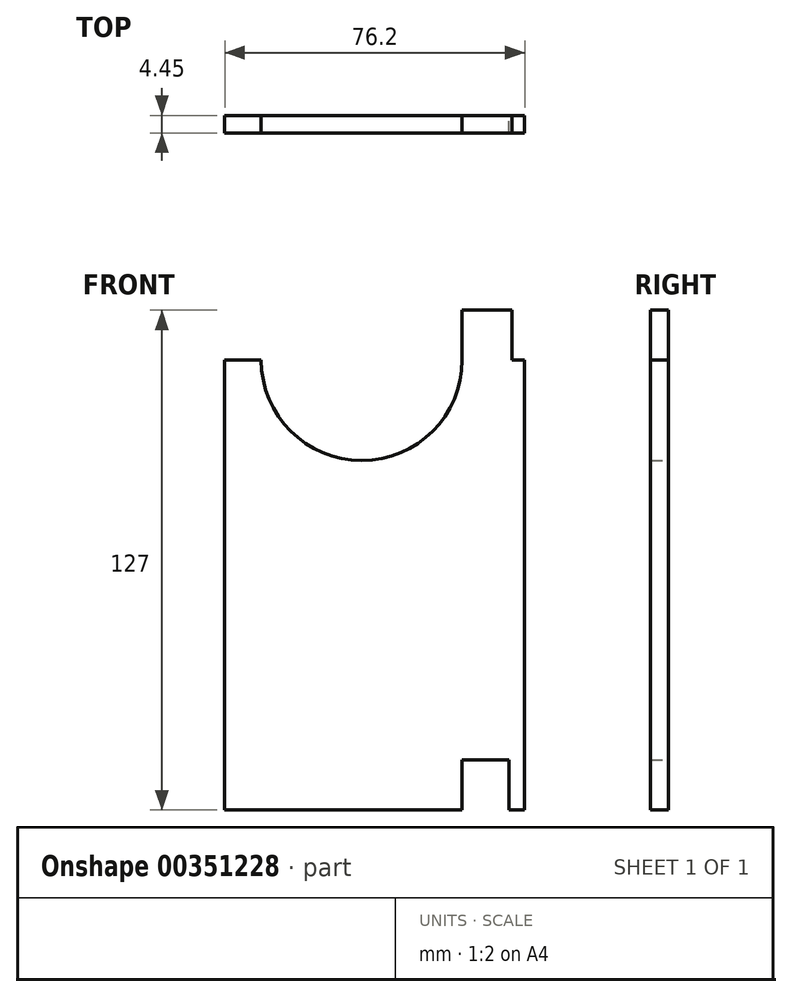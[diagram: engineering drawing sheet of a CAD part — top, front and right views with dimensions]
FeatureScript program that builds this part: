
annotation { "Feature Type Name" : "Feature", "Feature Type Description" : "" }
export const myFeature = defineFeature(function(context is Context, id is Id, definition is map)
    precondition{}
    {
        {
            var Q0;
            Q0=qCreatedBy(makeId("Front.planeOp"),FACE);
            var sketch = newSketch(context, id + "F0", { "sketchPlane" : qUnion([Q0])});
            skLineSegment(sketch, "E0", {"start": v(-43.64, 217.3) * mm, "end": v(-43.64, 103) * mm});
            skLineSegment(sketch, "E1", {"start": v(-43.64, 103) * mm, "end": v(16.68, 103) * mm});
            skLineSegment(sketch, "E2", {"start": v(32.56, 103) * mm, "end": v(32.56, 217.3) * mm});
            skLineSegment(sketch, "E3", {"start": v(32.56, 217.3) * mm, "end": v(29.38, 217.3) * mm});
            skLineSegment(sketch, "E4", {"start": v(16.68, 217.3) * mm, "end": v(16.68, 230) * mm});
            skLineSegment(sketch, "E5", {"start": v(16.68, 230) * mm, "end": v(29.38, 230) * mm});
            skLineSegment(sketch, "E6", {"start": v(29.38, 230) * mm, "end": v(29.38, 217.3) * mm});
            skLineSegment(sketch, "E7", {"start": v(-43.64, 217.3) * mm, "end": v(-34.37, 217.3) * mm});
            skArc(sketch, "E8", {"start": v(-34.37, 217.3) * mm, "mid": v(-8.84, 191.77) * mm, "end": v(16.68, 217.3) * mm});
            skLineSegment(sketch, "E9", {"start": v(32.56, 103) * mm, "end": v(29.38, 103) * mm});
            skLineSegment(sketch, "E10", {"start": v(16.68, 103) * mm, "end": v(16.68, 115.7) * mm});
            skLineSegment(sketch, "E11.trimOffspring", {"start": v(29.38, 103) * mm, "end": v(32.56, 103) * mm});
            skLineSegment(sketch, "E12", {"start": v(16.68, 115.7) * mm, "end": v(28.59, 115.7) * mm});
            skLineSegment(sketch, "E13", {"start": v(28.59, 115.7) * mm, "end": v(28.59, 103) * mm});
            skLineSegment(sketch, "E14", {"start": v(28.59, 103) * mm, "end": v(29.38, 103) * mm});
            skSolve(sketch);
        }
        {
            var Q0;
            Q0 = qSketchRegion(id + "F0", true);
            var Q1;
            Q1=makeQuery(id+"F0.imprint","IMPRINT",FACE,{"disambiguationData":[TD([[makeQuery(id+"F0.imprint","IMPRINT",EDGE,{"derivedFrom":sQuery(id+"F0.wireOp",EDGE,"E0")}),1.0]])]});
            extrude(context, id + "F1", {"entities" : qUnion([Q0, Q1]), "depth" : 4.44 * mm});
        }
    });
